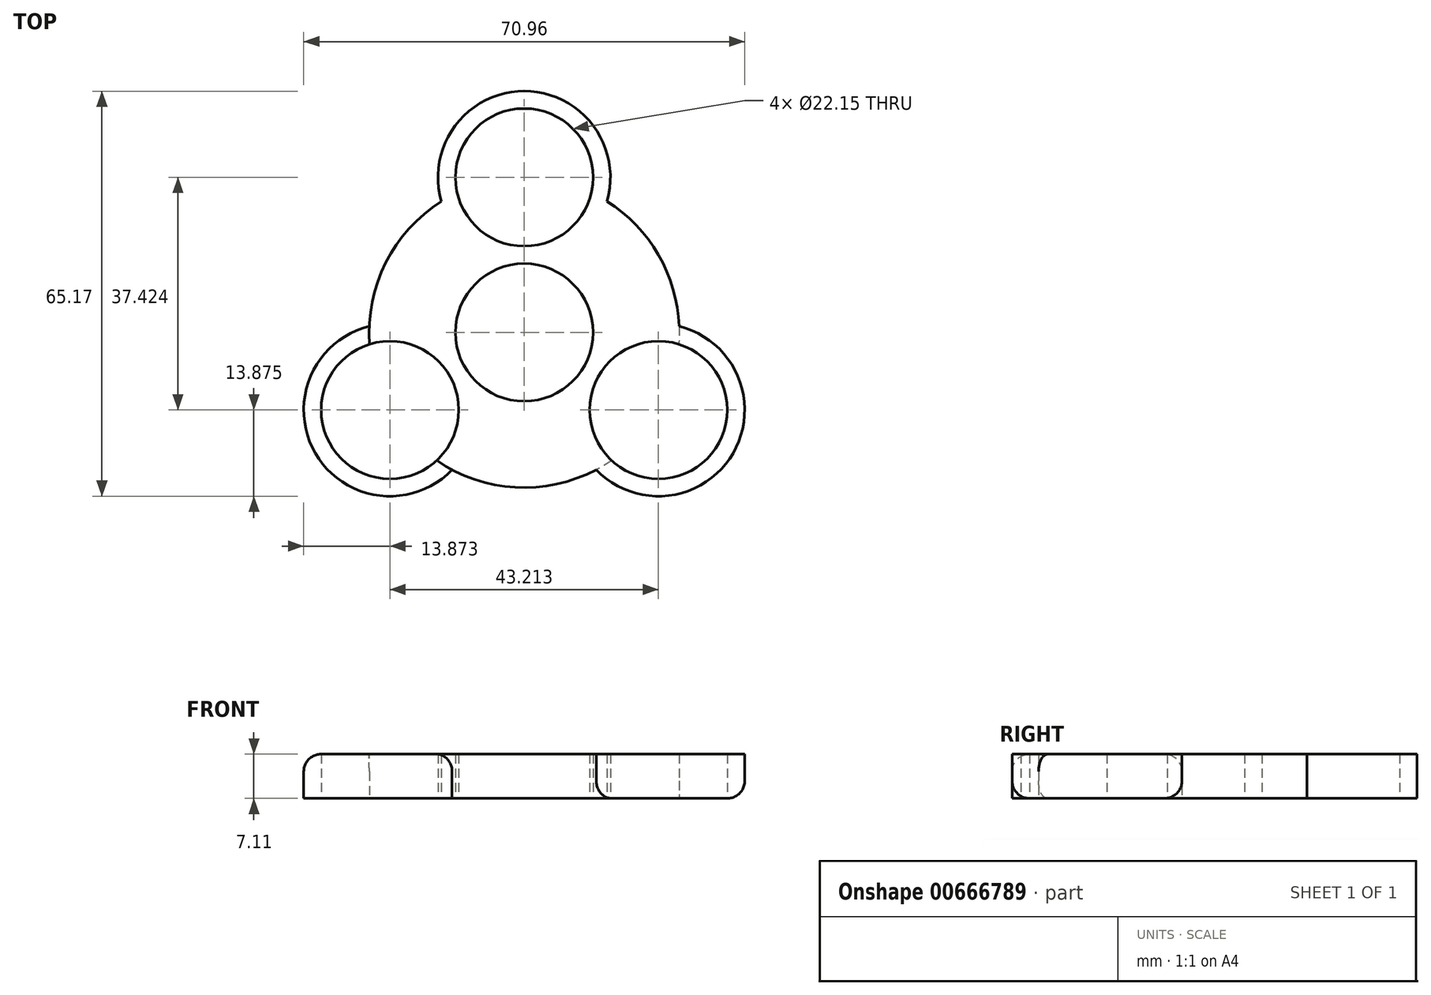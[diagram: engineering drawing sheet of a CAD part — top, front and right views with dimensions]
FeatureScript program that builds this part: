
annotation { "Feature Type Name" : "Feature", "Feature Type Description" : "" }
export const myFeature = defineFeature(function(context is Context, id is Id, definition is map)
    precondition{}
    {
        {
            var Q0;
            Q0=qCreatedBy(makeId("Top.planeOp"),FACE);
            var sketch = newSketch(context, id + "F0", { "sketchPlane" : qUnion([Q0])});
            skCircle(sketch, "E0", {"center": v(0, 0) * mm, "radius": 11.07 * mm});
            skCircle(sketch, "E1", {"center": v(0, 24.95) * mm, "radius": 11.07 * mm});
            skArc(sketch, "E2", {"start": v(12.02, 18.01) * mm, "mid": v(12.02, 6.94) * mm, "end": v(21.6, 1.4) * mm});
            skArc(sketch, "E3", {"start": v(-21.6, 1.4) * mm, "mid": v(-12.02, 6.94) * mm, "end": v(-12.02, 18.01) * mm});
            skArc(sketch, "E4", {"start": v(9.6, -19.41) * mm, "mid": v(0, -13.87) * mm, "end": v(-9.6, -19.41) * mm});
            skCircle(sketch, "E5", {"center": v(-21.6, -12.47) * mm, "radius": 11.07 * mm});
            skCircle(sketch, "E6", {"center": v(21.6, -12.47) * mm, "radius": 11.07 * mm});
            skArc(sketch, "E7", {"start": v(12.02, 18.01) * mm, "mid": v(0, 38.82) * mm, "end": v(-12.02, 18.01) * mm});
            skArc(sketch, "E8", {"start": v(9.6, -19.41) * mm, "mid": v(33.62, -19.41) * mm, "end": v(21.6, 1.4) * mm});
            skArc(sketch, "E9", {"start": v(-21.6, 1.4) * mm, "mid": v(-33.62, -19.41) * mm, "end": v(-9.6, -19.41) * mm});
            skCircle(sketch, "E10", {"center": v(0, 0) * mm, "radius": 24.95 * mm});
            skSolve(sketch);
        }
        {
            var Q0;
            Q0 = qSketchRegion(id + "F0", true);
            extrude(context, id + "F1", {"entities" : qUnion([Q0]), "depth" : 7.11 * mm, "offsetDistance" : 25.4 * mm});
        }
        {
            var Q0;
            Q0=makeQuery(id+"F1.opExtrude","CAP_EDGE",EDGE,{"disambiguationData":[OSD([sQuery(id+"F0.wireOp",EDGE,"E9")])],"isStart":false});
            fillet(context, id + "F2", {"entities" : qUnion([Q0]), "radius" : 2.8 * mm, "tangentPropagation" : true, "allowEdgeOverflow" : false});
        }
        {
            var Q0;
            Q0=makeQuery(id+"F1.opExtrude","CAP_EDGE",EDGE,{"disambiguationData":[OSD([sQuery(id+"F0.wireOp",EDGE,"E8")])],"isStart":true});
            fillet(context, id + "F3", {"entities" : qUnion([Q0]), "radius" : 2.8 * mm, "tangentPropagation" : true, "allowEdgeOverflow" : false});
        }
    });
